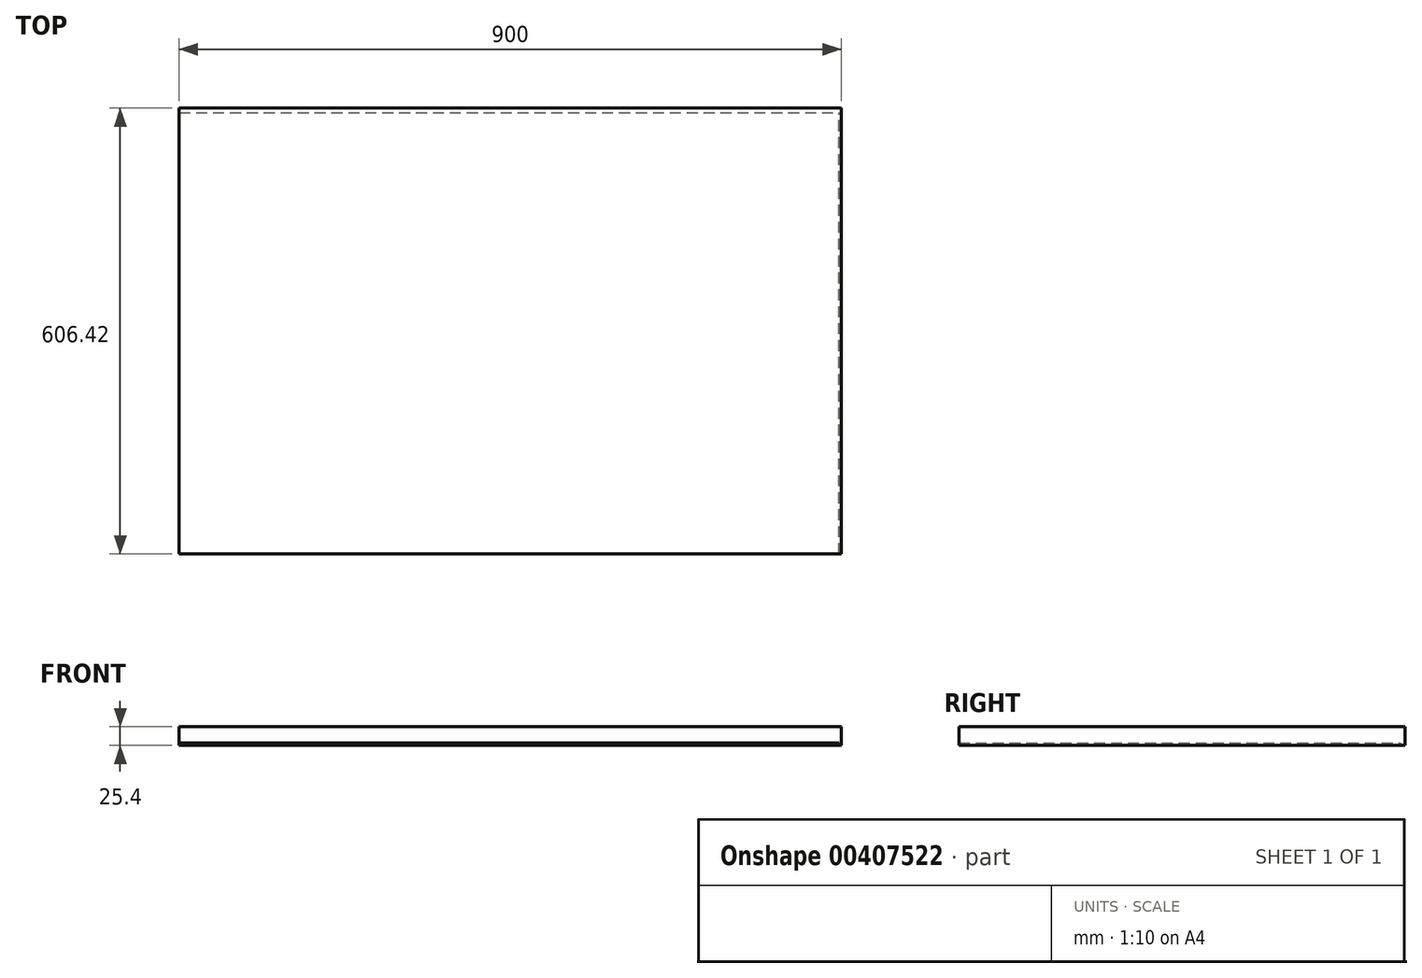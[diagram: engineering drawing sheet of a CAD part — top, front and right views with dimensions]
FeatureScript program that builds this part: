
annotation { "Feature Type Name" : "Feature", "Feature Type Description" : "" }
export const myFeature = defineFeature(function(context is Context, id is Id, definition is map)
    precondition{}
    {
        {
            var Q0;
            Q0=qCreatedBy(makeId("Top.planeOp"),FACE);
            var sketch = newSketch(context, id + "F0", { "sketchPlane" : qUnion([Q0])});
            skLineSegment(sketch, "E0.bottom", {"start": v(0, 0) * mm, "end": v(896.82, 0) * mm});
            skLineSegment(sketch, "E0.top", {"start": v(0, 600) * mm, "end": v(896.82, 600) * mm});
            skLineSegment(sketch, "E0.left", {"start": v(0, 0) * mm, "end": v(0, 600) * mm});
            skLineSegment(sketch, "E0.right", {"start": v(896.82, 0) * mm, "end": v(896.82, 600) * mm});
            skLineSegment(sketch, "E1.bottom", {"start": v(0, 0) * mm, "end": v(900, 0) * mm});
            skLineSegment(sketch, "E1.top", {"start": v(0, 606.42) * mm, "end": v(900, 606.42) * mm});
            skLineSegment(sketch, "E1.left", {"start": v(0, 0) * mm, "end": v(0, 606.42) * mm});
            skLineSegment(sketch, "E1.right", {"start": v(900, 0) * mm, "end": v(900, 606.42) * mm});
            skSolve(sketch);
        }
        {
            var Q0;
            {var subQ0=sQuery(id+"F0.wireOp",EDGE,"E0.top");Q0=makeQuery(id+"F0.imprint","IMPRINT",FACE,{"disambiguationData":[TD([[makeQuery(id+"F0.imprint","IMPRINT",EDGE,{"derivedFrom":subQ0}),-1.0]])]});}
            extrude(context, id + "F1", {"entities" : qUnion([Q0]), "depth" : 3.17 * mm, "offsetDistance" : 25.4 * mm});
        }
        {
            var Q0;
            {var subQ0=sQuery(id+"F0.wireOp",EDGE,"E0.top");Q0=makeQuery(id+"F0.imprint","IMPRINT",FACE,{"disambiguationData":[TD([[makeQuery(id+"F0.imprint","IMPRINT",EDGE,{"derivedFrom":subQ0}),-1.0]])]});}
            var Q1;
            {var subQ0=sQuery(id+"F0.wireOp",EDGE,"E0.top");Q1=makeQuery(id+"F0.imprint","IMPRINT",FACE,{"disambiguationData":[TD([[makeQuery(id+"F0.imprint","IMPRINT",EDGE,{"derivedFrom":subQ0}),1.0]])]});}
            extrude(context, id + "F2", {"entities" : qUnion([Q0, Q1]), "depth" : 25.4 * mm, "offsetDistance" : 25.4 * mm});
        }
    });
